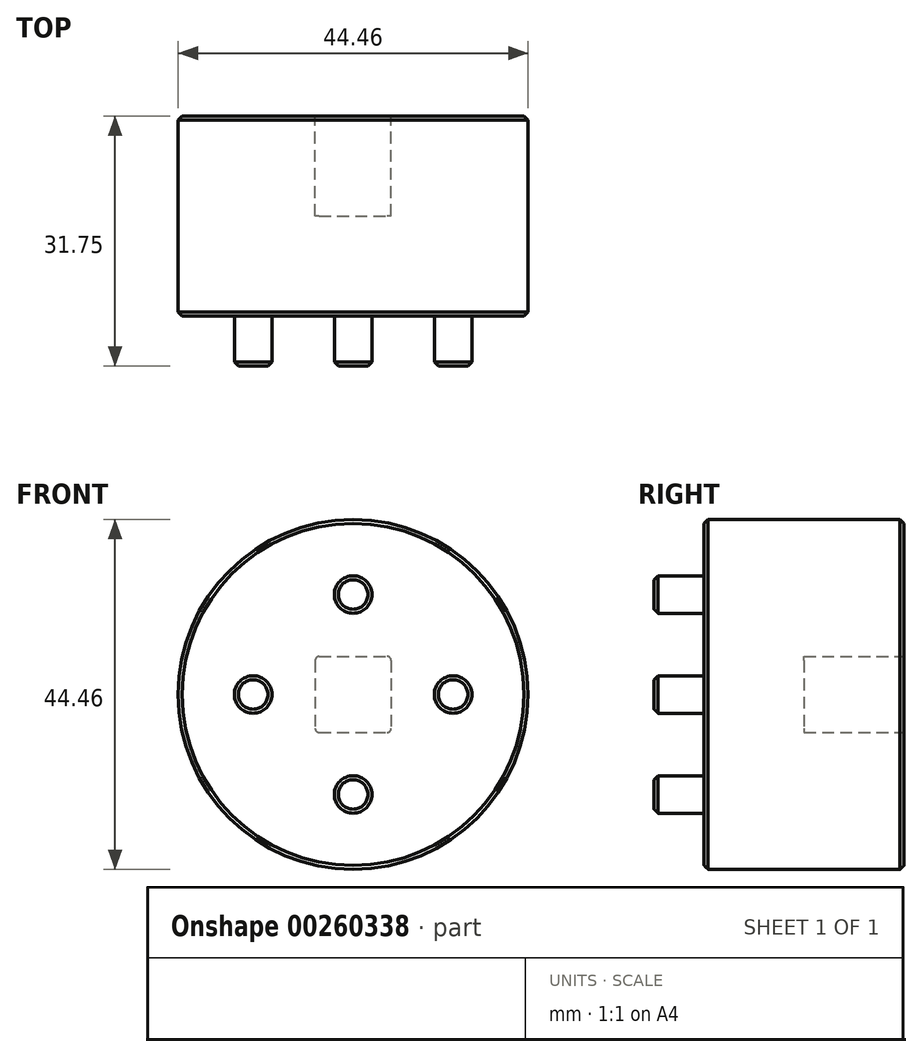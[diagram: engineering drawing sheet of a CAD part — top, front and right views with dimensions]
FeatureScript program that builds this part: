
annotation { "Feature Type Name" : "Feature", "Feature Type Description" : "" }
export const myFeature = defineFeature(function(context is Context, id is Id, definition is map)
    precondition{}
    {
        {
            var Q0;
            Q0=qCreatedBy(makeId("Front.planeOp"),FACE);
            var sketch = newSketch(context, id + "F0", { "sketchPlane" : qUnion([Q0])});
            skCircle(sketch, "E0", {"center": v(0, 0) * mm, "radius": 22.23 * mm});
            skSolve(sketch);
        }
        {
            var Q0;
            Q0 = qSketchRegion(id + "F0", true);
            extrude(context, id + "F1", {"entities" : qUnion([Q0]), "depth" : 25.4 * mm});
        }
        {
            var Q0;
            Q0=makeQuery(id+"F1.opExtrude","CAP_FACE",FACE,{"disambiguationData":[OSD([sQuery(id+"F0.wireOp",EDGE,"E0")])],"isStart":false});
            var sketch = newSketch(context, id + "F2", { "sketchPlane" : qUnion([Q0])});
            skCircle(sketch, "E1", {"center": v(0, 12.7) * mm, "radius": 2.38 * mm});
            skCircle(sketch, "E2.1.0", {"center": v(-12.7, 0) * mm, "radius": 2.38 * mm});
            skCircle(sketch, "E2.2.0", {"center": v(0, -12.7) * mm, "radius": 2.38 * mm});
            skCircle(sketch, "E2.3.0", {"center": v(12.7, 0) * mm, "radius": 2.38 * mm});
            skPoint(sketch, "E2.center", {"position": v(0, 0) * mm});
            skSolve(sketch);
        }
        {
            var Q0;
            Q0 = qSketchRegion(id + "F2", true);
            extrude(context, id + "F3", {"entities" : qUnion([Q0]), "operationType" : NewBodyOperationType.ADD, "depth" : 6.35 * mm});
        }
        {
            var Q0;
            Q0=makeQuery(id+"F1.opExtrude","CAP_FACE",FACE,{"disambiguationData":[OSD([sQuery(id+"F0.wireOp",EDGE,"E0")])],"isStart":true});
            var sketch = newSketch(context, id + "F4", { "sketchPlane" : qUnion([Q0])});
            skLineSegment(sketch, "E3.bottom", {"start": v(4.83, 4.83) * mm, "end": v(-4.83, 4.83) * mm});
            skLineSegment(sketch, "E3.top", {"start": v(4.83, -4.83) * mm, "end": v(-4.83, -4.83) * mm});
            skLineSegment(sketch, "E3.left", {"start": v(4.83, 4.83) * mm, "end": v(4.83, -4.83) * mm});
            skLineSegment(sketch, "E3.right", {"start": v(-4.83, 4.83) * mm, "end": v(-4.83, -4.83) * mm});
            skPoint(sketch, "E3.middle", {"position": v(0, 0) * mm});
            skSolve(sketch);
        }
        {
            var Q0;
            Q0 = qSketchRegion(id + "F4", true);
            extrude(context, id + "F5", {"entities" : qUnion([Q0]), "operationType" : NewBodyOperationType.REMOVE, "oppositeDirection" : true, "depth" : 12.7 * mm});
        }
        {
            var Q0;
            Q0=makeQuery(id+"F5.boolean.opBoolean","COPY",EDGE,{"derivedFrom":makeQuery(id+"F5.opExtrude","SWEPT_EDGE",EDGE,{"disambiguationData":[OSD([sQuery(id+"F4.wireOp",EDGE,"E3.top"),sQuery(id+"F4.wireOp",EDGE,"E3.left")])]})});
            var Q1;
            Q1=makeQuery(id+"F5.boolean.opBoolean","COPY",EDGE,{"derivedFrom":makeQuery(id+"F5.opExtrude","SWEPT_EDGE",EDGE,{"disambiguationData":[OSD([sQuery(id+"F4.wireOp",EDGE,"E3.bottom"),sQuery(id+"F4.wireOp",EDGE,"E3.left")])]})});
            var Q2;
            Q2=makeQuery(id+"F5.boolean.opBoolean","COPY",EDGE,{"derivedFrom":makeQuery(id+"F5.opExtrude","SWEPT_EDGE",EDGE,{"disambiguationData":[OSD([sQuery(id+"F4.wireOp",EDGE,"E3.bottom"),sQuery(id+"F4.wireOp",EDGE,"E3.right")])]})});
            var Q3;
            Q3=makeQuery(id+"F5.boolean.opBoolean","COPY",EDGE,{"derivedFrom":makeQuery(id+"F5.opExtrude","SWEPT_EDGE",EDGE,{"disambiguationData":[OSD([sQuery(id+"F4.wireOp",EDGE,"E3.top"),sQuery(id+"F4.wireOp",EDGE,"E3.right")])]})});
            fillet(context, id + "F6", {"entities" : qUnion([Q0, Q1, Q2, Q3]), "radius" : 0.5 * mm, "tangentPropagation" : true, "allowEdgeOverflow" : false});
        }
        {
            var Q0;
            Q0=makeQuery(id+"F5.boolean.opBoolean","COPY",EDGE,{"derivedFrom":makeQuery(id+"F5.opExtrude","CAP_EDGE",EDGE,{"disambiguationData":[OSD([sQuery(id+"F4.wireOp",EDGE,"E3.top")])],"isStart":true})});
            var Q1;
            Q1=makeQuery(id+"F1.opExtrude","CAP_EDGE",EDGE,{"disambiguationData":[OSD([sQuery(id+"F0.wireOp",EDGE,"E0")])],"isStart":true});
            var Q2;
            Q2=makeQuery(id+"F1.opExtrude","CAP_EDGE",EDGE,{"disambiguationData":[OSD([sQuery(id+"F0.wireOp",EDGE,"E0")])],"isStart":false});
            var Q3;
            Q3=makeQuery(id+"F3.opExtrude","CAP_EDGE",EDGE,{"disambiguationData":[OSD([sQuery(id+"F2.wireOp",EDGE,"E2.1.0")])],"isStart":false});
            var Q4;
            Q4=makeQuery(id+"F3.opExtrude","CAP_EDGE",EDGE,{"disambiguationData":[OSD([sQuery(id+"F2.wireOp",EDGE,"E1")])],"isStart":false});
            var Q5;
            Q5=makeQuery(id+"F3.opExtrude","CAP_EDGE",EDGE,{"disambiguationData":[OSD([sQuery(id+"F2.wireOp",EDGE,"E2.3.0")])],"isStart":false});
            var Q6;
            Q6=makeQuery(id+"F3.opExtrude","CAP_EDGE",EDGE,{"disambiguationData":[OSD([sQuery(id+"F2.wireOp",EDGE,"E2.2.0")])],"isStart":false});
            chamfer(context, id + "F7", {"entities" : qUnion([Q0, Q1, Q2, Q3, Q4, Q5, Q6]), "width" : 0.5 * mm, "tangentPropagation" : true});
        }
    });
